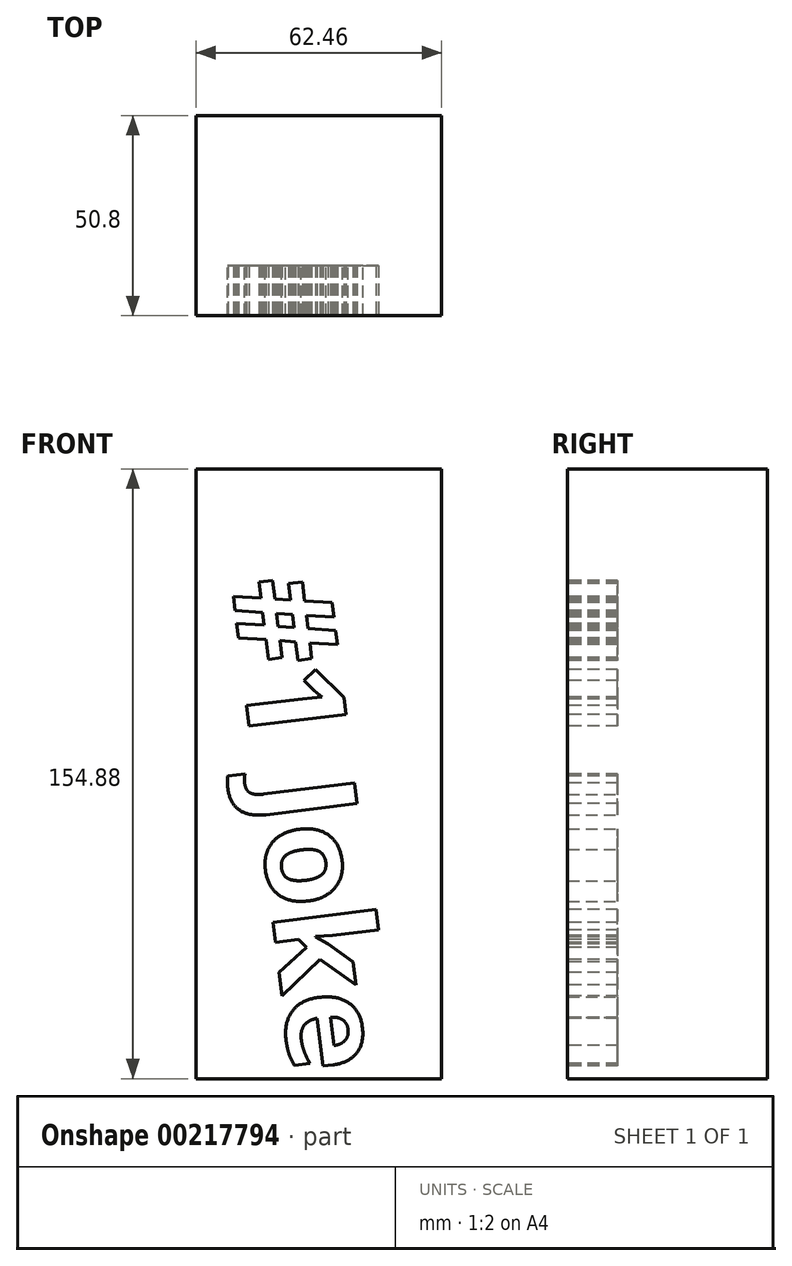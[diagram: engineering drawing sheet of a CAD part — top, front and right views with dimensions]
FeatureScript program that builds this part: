
annotation { "Feature Type Name" : "Feature", "Feature Type Description" : "" }
export const myFeature = defineFeature(function(context is Context, id is Id, definition is map)
    precondition{}
    {
        {
            var Q0;
            Q0=qCreatedBy(makeId("Front.planeOp"),FACE);
            var sketch = newSketch(context, id + "F0", { "sketchPlane" : qUnion([Q0])});
            skLineSegment(sketch, "E0.bottom", {"start": v(-38.8, 75.73) * mm, "end": v(23.67, 75.73) * mm});
            skLineSegment(sketch, "E0.top", {"start": v(-38.8, -79.15) * mm, "end": v(23.67, -79.15) * mm});
            skLineSegment(sketch, "E0.left", {"start": v(-38.8, 75.73) * mm, "end": v(-38.8, -79.15) * mm});
            skLineSegment(sketch, "E0.right", {"start": v(23.67, 75.73) * mm, "end": v(23.67, -79.15) * mm});
            skSolve(sketch);
        }
        {
            var Q0;
            Q0=makeQuery(id+"F0.imprint","IMPRINT",FACE,{"disambiguationData":[TD([[makeQuery(id+"F0.imprint","IMPRINT",EDGE,{"derivedFrom":sQuery(id+"F0.wireOp",EDGE,"E0.bottom")}),-1.0]])]});
            extrude(context, id + "F1", {"entities" : qUnion([Q0]), "depth" : 50.8 * mm});
        }
        {
            var Q0;
            Q0=makeQuery(id+"F1.opExtrude","CAP_FACE",FACE,{"disambiguationData":[OSD([sQuery(id+"F0.wireOp",EDGE,"E0.bottom"),sQuery(id+"F0.wireOp",EDGE,"E0.top"),sQuery(id+"F0.wireOp",EDGE,"E0.left"),sQuery(id+"F0.wireOp",EDGE,"E0.right")])],"isStart":false});
            var sketch = newSketch(context, id + "F2", { "sketchPlane" : qUnion([Q0])});
            skText(sketch, "E1", { "text": "#1 Joke", "fontName": "OpenSans-Bold.ttf"});
            const initialGuessF2  = {"E1": [-0.02969, 0.04691, 0.12097, -0.99266, 0.02499]};
            skSetInitialGuess(sketch, initialGuessF2);
            skSolve(sketch);
        }
        {
            var Q0;
            Q0 = qSketchRegion(id + "F2", true);
            extrude(context, id + "F3", {"entities" : qUnion([Q0]), "operationType" : NewBodyOperationType.REMOVE, "oppositeDirection" : true, "depth" : 12.7 * mm});
        }
    });
